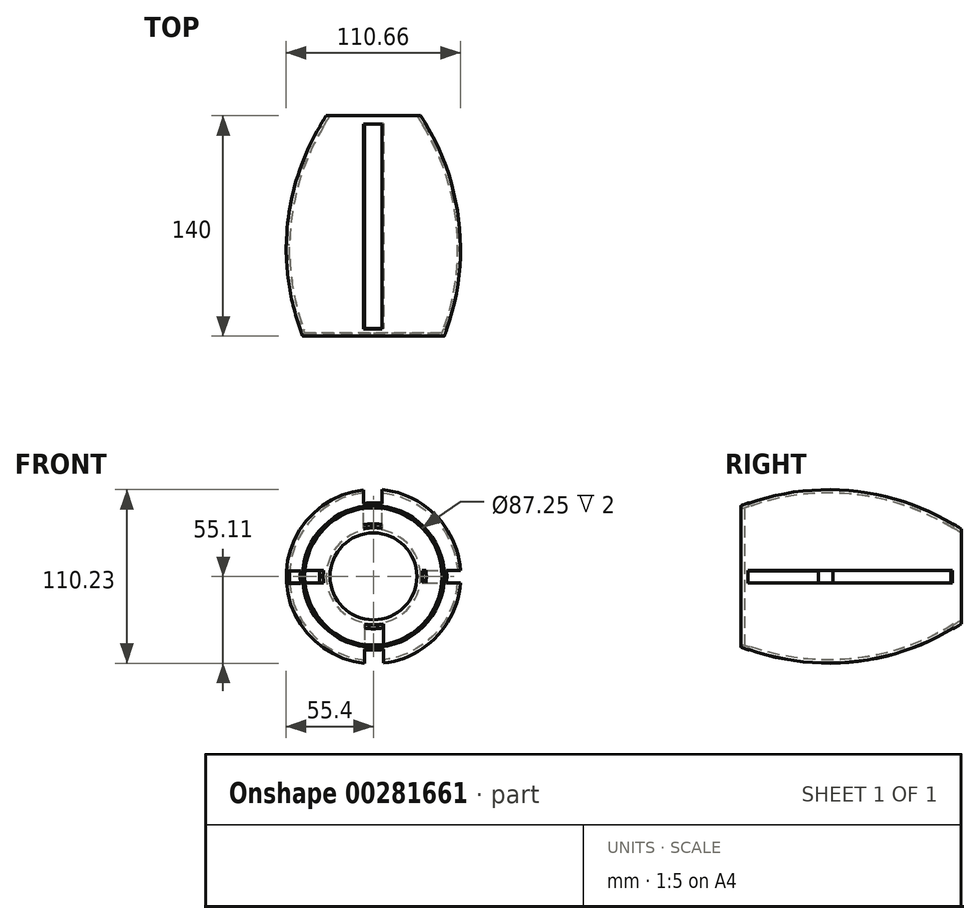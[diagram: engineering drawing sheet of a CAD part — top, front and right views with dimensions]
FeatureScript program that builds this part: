
annotation { "Feature Type Name" : "Feature", "Feature Type Description" : "" }
export const myFeature = defineFeature(function(context is Context, id is Id, definition is map)
    precondition{}
    {
        {
            var Q0;
            Q0=qCreatedBy(makeId("Top.planeOp"),FACE);
            var sketch = newSketch(context, id + "F0", { "sketchPlane" : qUnion([Q0])});
            skLineSegment(sketch, "E0", {"start": v(0, 0) * mm, "end": v(-30, 0) * mm});
            skArc(sketch, "E1", {"start": v(-30, 0) * mm, "mid": v(-54.52, -68.18) * mm, "end": v(-45, -140) * mm});
            skLineSegment(sketch, "E2", {"start": v(-45, -140) * mm, "end": v(0, -140) * mm});
            skLineSegment(sketch, "E3", {"start": v(0, -140) * mm, "end": v(0, 0) * mm});
            skSolve(sketch);
        }
        {
            var Q0;
            Q0 = qSketchRegion(id + "F0", true);
            var Q1;
            Q1=sQuery(id+"F0.wireOp",EDGE,"E3");
            revolve(context, id + "F1", {"entities" : qUnion([Q0]), "axis" : qUnion([Q1]), "revolveType" : RevolveType.FULL});
        }
        {
            var Q0;
            Q0=makeQuery(id+"F1.opRevolve","SWEPT_FACE",FACE,{"disambiguationData":[OSD([sQuery(id+"F0.wireOp",EDGE,"E0")])]});
            shell(context, id + "F2", {"entities" : qUnion([Q0]), "thickness" : 2 * mm});
        }
        {
            var Q0;
            Q0=makeQuery(id+"F2.opShell","OFFSET_FACE",FACE,{"disambiguationData":[OSD([sQuery(id+"F0.wireOp",EDGE,"E2")])]});
            extrude(context, id + "F3", {"entities" : qUnion([Q0]), "operationType" : NewBodyOperationType.REMOVE, "endBound" : BoundingType.THROUGH_ALL, "oppositeDirection" : true, "depth" : 25 * mm});
        }
        {
            var Q0;
            Q0=qCreatedBy(makeId("Top.planeOp"),FACE);
            var sketch = newSketch(context, id + "F4", { "sketchPlane" : qUnion([Q0])});
            skLineSegment(sketch, "E4.bottom", {"start": v(-6.44, -5.32) * mm, "end": v(5.56, -5.32) * mm});
            skLineSegment(sketch, "E4.top", {"start": v(-6.44, -135.32) * mm, "end": v(5.56, -135.32) * mm});
            skLineSegment(sketch, "E4.left", {"start": v(-6.44, -5.32) * mm, "end": v(-6.44, -135.32) * mm});
            skLineSegment(sketch, "E4.right", {"start": v(5.56, -5.32) * mm, "end": v(5.56, -135.32) * mm});
            skSolve(sketch);
        }
        {
            var Q0;
            Q0 = qSketchRegion(id + "F4", true);
            extrude(context, id + "F5", {"entities" : qUnion([Q0]), "operationType" : NewBodyOperationType.REMOVE, "endBound" : BoundingType.THROUGH_ALL, "depth" : 25 * mm});
        }
        {
            var Q0;
            Q0=qCreatedBy(makeId("Right.planeOp"),FACE);
            var sketch = newSketch(context, id + "F6", { "sketchPlane" : qUnion([Q0])});
            skLineSegment(sketch, "E5.bottom", {"start": v(-5.7, 3.83) * mm, "end": v(-135.7, 3.83) * mm});
            skLineSegment(sketch, "E5.top", {"start": v(-5.7, -4.17) * mm, "end": v(-135.7, -4.17) * mm});
            skLineSegment(sketch, "E5.left", {"start": v(-5.7, 3.83) * mm, "end": v(-5.7, -4.17) * mm});
            skLineSegment(sketch, "E5.right", {"start": v(-135.7, 3.83) * mm, "end": v(-135.7, -4.17) * mm});
            skSolve(sketch);
        }
        {
            var Q0;
            Q0 = qSketchRegion(id + "F6", true);
            extrude(context, id + "F7", {"entities" : qUnion([Q0]), "operationType" : NewBodyOperationType.REMOVE, "endBound" : BoundingType.THROUGH_ALL, "depth" : 25 * mm});
        }
        {
            var Q0;
            Q0=qCreatedBy(makeId("Top.planeOp"),FACE);
            var sketch = newSketch(context, id + "F8", { "sketchPlane" : qUnion([Q0])});
            skLineSegment(sketch, "E6.bottom", {"start": v(6.38, -5.12) * mm, "end": v(-5.62, -5.12) * mm});
            skLineSegment(sketch, "E6.top", {"start": v(6.38, -135.12) * mm, "end": v(-5.62, -135.12) * mm});
            skLineSegment(sketch, "E6.left", {"start": v(6.38, -5.12) * mm, "end": v(6.38, -135.12) * mm});
            skLineSegment(sketch, "E6.right", {"start": v(-5.62, -5.12) * mm, "end": v(-5.62, -135.12) * mm});
            skSolve(sketch);
        }
        {
            var Q0;
            Q0 = qSketchRegion(id + "F8", true);
            extrude(context, id + "F9", {"entities" : qUnion([Q0]), "operationType" : NewBodyOperationType.REMOVE, "endBound" : BoundingType.THROUGH_ALL, "oppositeDirection" : true, "depth" : 25 * mm});
        }
        {
            var Q0;
            Q0=qCreatedBy(makeId("Right.planeOp"),FACE);
            var sketch = newSketch(context, id + "F10", { "sketchPlane" : qUnion([Q0])});
            skLineSegment(sketch, "E7.bottom", {"start": v(-6.75, -4.23) * mm, "end": v(-81.75, -4.23) * mm});
            skLineSegment(sketch, "E7.top", {"start": v(-6.75, 3.77) * mm, "end": v(-81.75, 3.77) * mm});
            skLineSegment(sketch, "E7.left", {"start": v(-6.75, -4.23) * mm, "end": v(-6.75, 3.77) * mm});
            skLineSegment(sketch, "E7.right", {"start": v(-81.75, -4.23) * mm, "end": v(-81.75, 3.77) * mm});
            skLineSegment(sketch, "E8.bottom", {"start": v(-91, -4.37) * mm, "end": v(-136, -4.37) * mm});
            skLineSegment(sketch, "E8.top", {"start": v(-91, 3.63) * mm, "end": v(-136, 3.63) * mm});
            skLineSegment(sketch, "E8.left", {"start": v(-91, -4.37) * mm, "end": v(-91, 3.63) * mm});
            skLineSegment(sketch, "E8.right", {"start": v(-136, -4.37) * mm, "end": v(-136, 3.63) * mm});
            skSolve(sketch);
        }
        {
            var Q0;
            Q0 = qSketchRegion(id + "F10", true);
            extrude(context, id + "F11", {"entities" : qUnion([Q0]), "operationType" : NewBodyOperationType.REMOVE, "endBound" : BoundingType.THROUGH_ALL, "oppositeDirection" : true, "depth" : 25 * mm});
        }
    });
